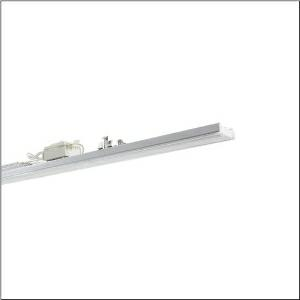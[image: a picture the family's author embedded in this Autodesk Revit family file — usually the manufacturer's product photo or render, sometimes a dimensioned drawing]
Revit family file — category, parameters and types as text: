
# Revit family: licross_r__21_recessed_mo_52tl11dv4fxg_3abc
name_source: partatom
category: Lighting Fixtures
units: mm (PartAtom-declared; Revit-internal decimal feet)

## family parameters
Cut with Voids When Loaded = No
Host = Face
Light Source = No
Part Type = Normal
Room Calculation Point = No
Round Connector Dimension = Use Diameter
Shared = No

## types (1)
- --- (1 x LED, 15180 lm, 85.3 W, 4000K)
    Apparent Load = 85 VA
    CIE Flux Codes = 89 96 99 100 100
    Color Rendering = 80
    Color Temperature = 4000K
    Default Elevation = 1800 mm
    Description = Licross® 21 Recessed MO, luminaire insert, of sheet steel, galvanised, coil coated, white, length: 2.250mm, width: 66mm, height: 67mm, LED rated luminous flux: 15.180lm, light colour: 840, control gear: DALI 2, with plug, 5-pole, with phase selection, mains connection: 220..240V, AC, 50/60Hz, rated input power: 85W, halogen-free wiring, primary light control with lens, of plastic, primary optical cover: cover, of PMMA, light emission: direct distribution, primary light characteristic: symmetric, protection rating (complete): IP40, insulation class (complete): insulation class I (protective earthing), certification: CE, ENEC, VDE, UKCA, protection symbol: D if used in an environment without relevant dust loads with corresponding accessories, impact resistance: IK06, permissible ambient temperature for indoor applications: -25..+35°C, corresponds to IFS (International Featured Standards) requirements for safety and quality in the food industry, reducing of maximum allowable ambient temperature of 5°C with ceiling mounting, LABS conformity tested according to VDMA 24364:2018-05, packaging unit: 1 piece
    Height = 58 mm
    Lamp = 1 x LED
    Lamp Light Flux = 15180 lm
    Lamp Power = 85.3 W
    Lamp count = 1
    Length = 2250 mm
    Luminous efficacy = 178 lm/W
    Manufacturer = Siteco
    ModVariant = No
    Model = 52TL11DV4FXG
    Mounting Place = Ceiling
    Mounting Type = Pendant
    Number of Poles = 1
    OnlyDefault = Yes
    Power Factor = 1
    Product Name = Licross® 21 Recessed MO
    Product group = luminaire insert
    ProductGroupID = 902
    Protection Class = Protection class I
    Protection Degree = IP 40
    RLX_Detail_Level = 1
    RLX_Emergency_Light_Flux = 0 lm
    RLX_Emergency_Type = 0
    RLX_Emergency_Type_DB = No
    RlxData = <blob elided: 29725 chars, md5=8cf297aa>
    Socket = socket
    Standby Power = 0 W
    System Light Flux = 15180 lm
    System Power = 85 W
    Type Comments = factory setting: luminous flux: 100 % | dim-lin: 254 | 390 mA
    Type Image = l_1296930.jpg
    URL = http://relux.com
    VarID = @adj_127092
    Voltage = 0 V
    Weight = 0.00 kg
    Width = 66 mm

## geometry (parser evidence)
native form markers: Blend x4, Sweep x10
no freeform markers — native parametric forms only
